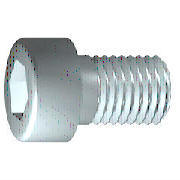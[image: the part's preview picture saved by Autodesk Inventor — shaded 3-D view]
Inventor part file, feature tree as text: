
AUTODESK INVENTOR PART (.ipt)
format: ipt  version: 2022 (Build 260153000, 153)  size: 190,976 bytes
history: native  units: mm (DEFAULTED — no unit token found)
features: sketch x2, extrude x1, plane x1, fillet x1
ambient origin geometry x7: Origin, YZ Plane, XY Plane, X Axis, Y Axis, Z Axis, Center Point
bodies: Solid1 (feature_tree), Body (feature_tree)
feature tree (5):
  extrude  "Slot"  Depth=3.0mm
  plane  "Work Plane1"
  fillet  "Fillet2"  Radius=3.0mm
  sketch  "Sketch1"  dims[d1=14.75mm d2=0.306825mm d3=3.0mm]
  sketch  "Sketch2"  dims[d4=1.3mm d5=60.0deg d6=3.0mm d7=3.0mm d8=2.886751mm d9=5.5mm d10=90.0deg d11=10.0mm d12=0.0mm d13=14.75mm d14=0.0mm d15=0.306725mm d16=0.306725mm d17=0.3mm d19=0.0mm d26=16.0mm d27=45.0deg d28=0.0mm d29=0.0mm d30=0.1mm]
